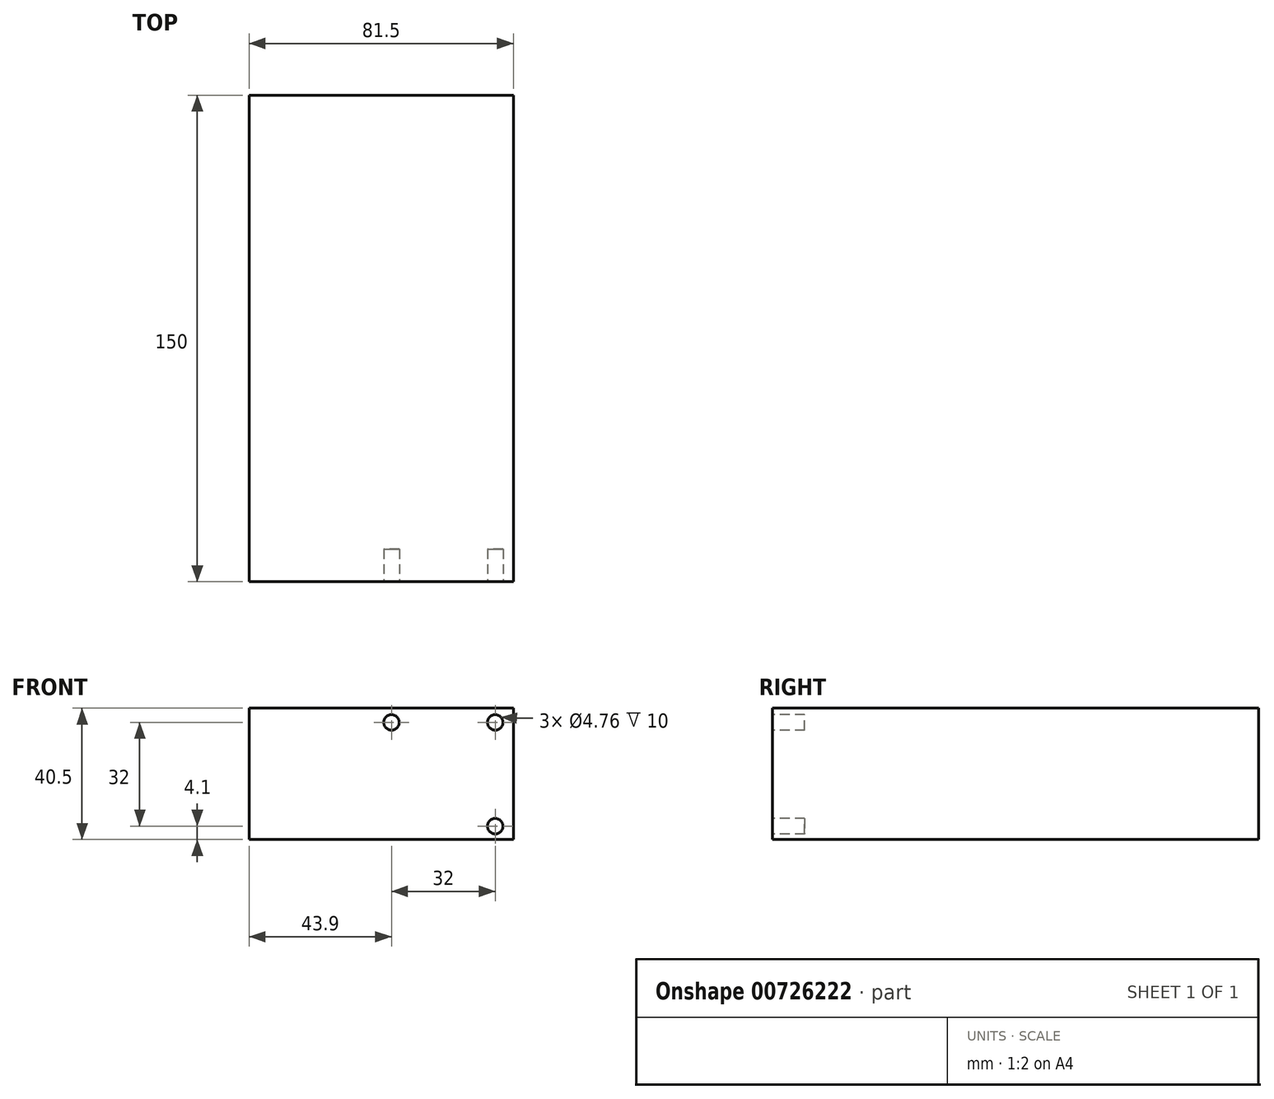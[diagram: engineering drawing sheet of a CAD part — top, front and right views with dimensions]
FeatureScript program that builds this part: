
annotation { "Feature Type Name" : "Feature", "Feature Type Description" : "" }
export const myFeature = defineFeature(function(context is Context, id is Id, definition is map)
    precondition{}
    {
        {
            var Q0;
            Q0=qCreatedBy(makeId("Top.planeOp"),FACE);
            var sketch = newSketch(context, id + "F0", { "sketchPlane" : qUnion([Q0])});
            skLineSegment(sketch, "E0.bottom", {"start": v(40.75, -75) * mm, "end": v(-40.75, -75) * mm});
            skLineSegment(sketch, "E0.top", {"start": v(40.75, 75) * mm, "end": v(-40.75, 75) * mm});
            skLineSegment(sketch, "E0.left", {"start": v(40.75, -75) * mm, "end": v(40.75, 75) * mm});
            skLineSegment(sketch, "E0.right", {"start": v(-40.75, -75) * mm, "end": v(-40.75, 75) * mm});
            skPoint(sketch, "E0.middle", {"position": v(0, 0) * mm});
            skSolve(sketch);
        }
        {
            var Q0;
            Q0 = qSketchRegion(id + "F0", true);
            extrude(context, id + "F1", {"entities" : qUnion([Q0]), "depth" : 40.5 * mm, "offsetDistance" : 25 * mm});
        }
        {
            var Q0;
            Q0=makeQuery(id+"F1.opExtrude","SWEPT_FACE",FACE,{"disambiguationData":[OSD([sQuery(id+"F0.wireOp",EDGE,"E0.bottom")])]});
            var sketch = newSketch(context, id + "F2", { "sketchPlane" : qUnion([Q0])});
            skCircle(sketch, "E1", {"center": v(35.15, 36.1) * mm, "radius": 2.38 * mm});
            skCircle(sketch, "E2", {"center": v(35.15, 4.1) * mm, "radius": 2.38 * mm});
            skLineSegment(sketch, "E3", {"start": v(35.15, 36.1) * mm, "end": v(35.15, 4.1) * mm, "construction": true});
            skCircle(sketch, "E4", {"center": v(3.15, 36.1) * mm, "radius": 2.38 * mm});
            skLineSegment(sketch, "E5", {"start": v(3.15, 36.1) * mm, "end": v(35.15, 36.1) * mm, "construction": true});
            skSolve(sketch);
        }
        {
            var Q0;
            Q0 = qSketchRegion(id + "F2", true);
            extrude(context, id + "F3", {"entities" : qUnion([Q0]), "operationType" : NewBodyOperationType.REMOVE, "oppositeDirection" : true, "depth" : 10 * mm, "offsetDistance" : 25 * mm});
        }
    });
